# Revit family: 56616 PRESTO NEW TOUCH
name_source: partatom
category: Appareils sanitaires
units: mm (PartAtom-declared; Revit-internal decimal feet)

## family parameters
Basée sur le plan de construction = Oui
Cote de connecteur circulaire = Utiliser le diamètre
Couper avec des vides une fois chargée = Non
Partagée = Oui
Point de calcul de pièce = Non
Toujours verticalement = Oui
Type d'élément = Normal

## types (1)
- 56616 PRESTO NEW TOUCH
    Arrivée d'eau = G 3/8"
    BOSUseNativeGeometries = 1
    Debit = 3 l/min
    Description = Robinet mitigeur sensitif pour lavabo sur plage avec alimentation 230V sans robinet d'arrêt droit - capot tournesol
    Elévation par défaut = 1219 mm
    Fabricant = LES ROBINETS PRESTO S.A.
    Famille produit = Lavabo
    Groupe produit = Sensitif
    Hauteur = 172 mm  [stored 0.564304 ft]
    Longueur = 158 mm
    Materiau principal = Laiton
    Materiau secondaire = Chrome
    Modèle = 56616 PRESTO NEW TOUCH
    Nom du fabricant = Presto
    Pays designer = France
    Pays fabricant = France
    Poids Net (Kg) = 0
    Product SKU = 56616
    Profondeur = 58 mm  [stored 0.190289 ft]
    Temps d'ecoulement = 6s
    UNSPSC Code = 301815
    URL = http://www.prestodatashare.com

note: [stored X ft] marks values corroborated as IEEE doubles in the binary element streams (Revit-internal decimal feet)

## geometry (parser evidence)
native form markers: Blend x1, Sweep x1
no freeform markers — native parametric forms only
